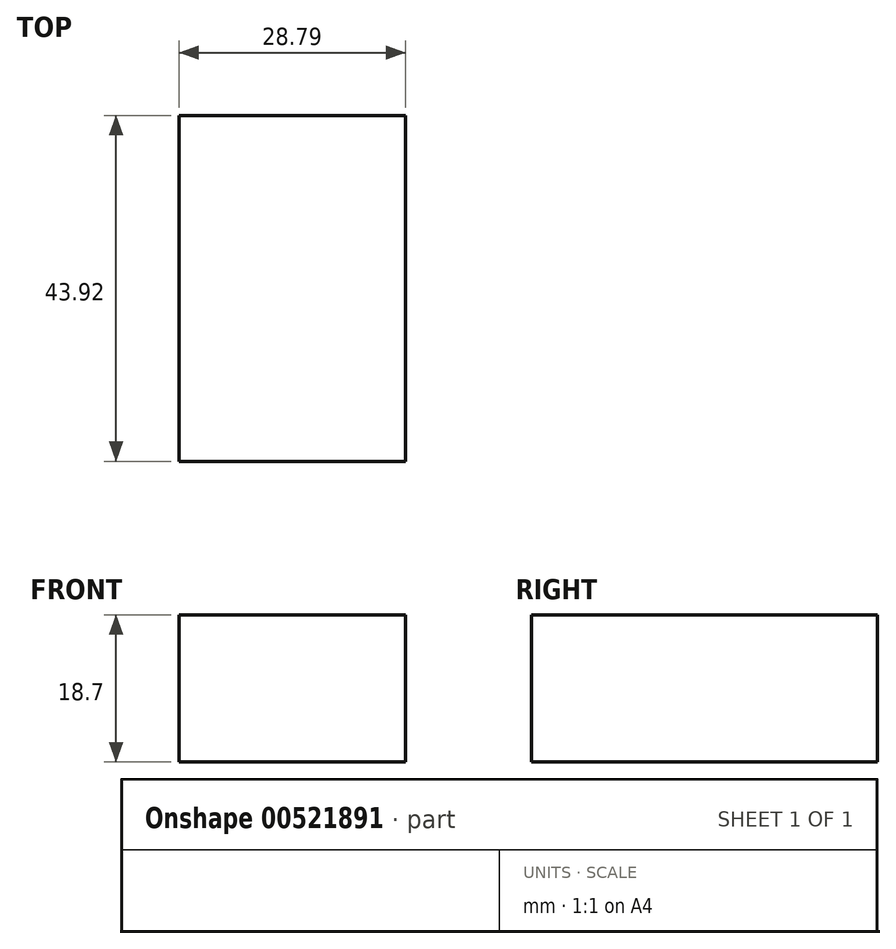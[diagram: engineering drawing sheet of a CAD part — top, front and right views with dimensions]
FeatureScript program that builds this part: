
annotation { "Feature Type Name" : "Feature", "Feature Type Description" : "" }
export const myFeature = defineFeature(function(context is Context, id is Id, definition is map)
    precondition{}
    {
        {
            var Q0;
            Q0=qCreatedBy(makeId("Front.planeOp"),FACE);
            var sketch = newSketch(context, id + "F0", { "sketchPlane" : qUnion([Q0])});
            skLineSegment(sketch, "E0.bottom", {"start": v(-36.91, 31.3) * mm, "end": v(63.09, 31.3) * mm});
            skLineSegment(sketch, "E0.top", {"start": v(-36.91, -18.7) * mm, "end": v(63.09, -18.7) * mm});
            skLineSegment(sketch, "E0.left", {"start": v(-36.91, 31.3) * mm, "end": v(-36.91, -18.7) * mm});
            skLineSegment(sketch, "E0.right", {"start": v(63.09, 31.3) * mm, "end": v(63.09, -18.7) * mm});
            skSolve(sketch);
        }
        {
            var Q0;
            Q0 = qSketchRegion(id + "F0", true);
            extrude(context, id + "F1", {"entities" : qUnion([Q0]), "depth" : 156 * mm, "offsetDistance" : 25 * mm});
        }
        {
            var Q0;
            Q0=qCreatedBy(makeId("Top.planeOp"),FACE);
            var sketch = newSketch(context, id + "F2", { "sketchPlane" : qUnion([Q0])});
            skLineSegment(sketch, "E1.bottom", {"start": v(-37.23, -62.74) * mm, "end": v(-8.12, -62.74) * mm});
            skLineSegment(sketch, "E1.top", {"start": v(-37.23, -18.82) * mm, "end": v(-8.12, -18.82) * mm});
            skLineSegment(sketch, "E1.left", {"start": v(-37.23, -62.74) * mm, "end": v(-37.23, -18.82) * mm});
            skLineSegment(sketch, "E1.right", {"start": v(-8.12, -62.74) * mm, "end": v(-8.12, -18.82) * mm});
            skSolve(sketch);
        }
        {
            var Q0;
            Q0 = qSketchRegion(id + "F2", true);
            extrude(context, id + "F3", {"entities" : qUnion([Q0]), "operationType" : NewBodyOperationType.INTERSECT, "endBound" : BoundingType.THROUGH_ALL, "oppositeDirection" : true, "depth" : 143 * mm, "offsetDistance" : 25 * mm});
        }
    });
